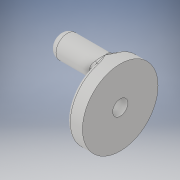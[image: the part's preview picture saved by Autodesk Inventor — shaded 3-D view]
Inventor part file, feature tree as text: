
AUTODESK INVENTOR PART (.ipt)
format: ipt  version: 2019 (Build 230136000, 136)  size: 178,688 bytes
history: native  units: in
note: dims shown in document units (in); Inventor stores cm internally (conversion verified against a paired STEP export)
features: fillet x3, sketch x2, revolve x1, extrude x1
ambient origin geometry x8: Origin, YZ Plane, XZ Plane, XY Plane, X Axis, Y Axis, Z Axis, Center Point
bodies: Solid1 (feature_tree)
feature tree (7):
  revolve  "Revolution1"  [1 undecoded]
  extrude  "Extrusion1"  Depth=0.3937in
  fillet  "Fillet1"  Radius=0.3937in
  fillet  "Fillet2"  [1 undecoded]
  fillet  "Fillet3"  Radius=0.5906in
  sketch  "Sketch1"  dims[d1=0.7874in d2=0.3937in]
  sketch  "Sketch2"  dims[d3=0.1969in d4=0.3937in d5=0.3937in d6=90.0deg d7=0.5906in d8=1.1811in d9=0.0in d10=0.0787in d11=0.1969in d12=0.1181in]
note: 2 required parameter values undecoded (feature->parameter linkage not recoverable at this tier; creation-order binding heuristic only, values carry confidence <= 0.55)